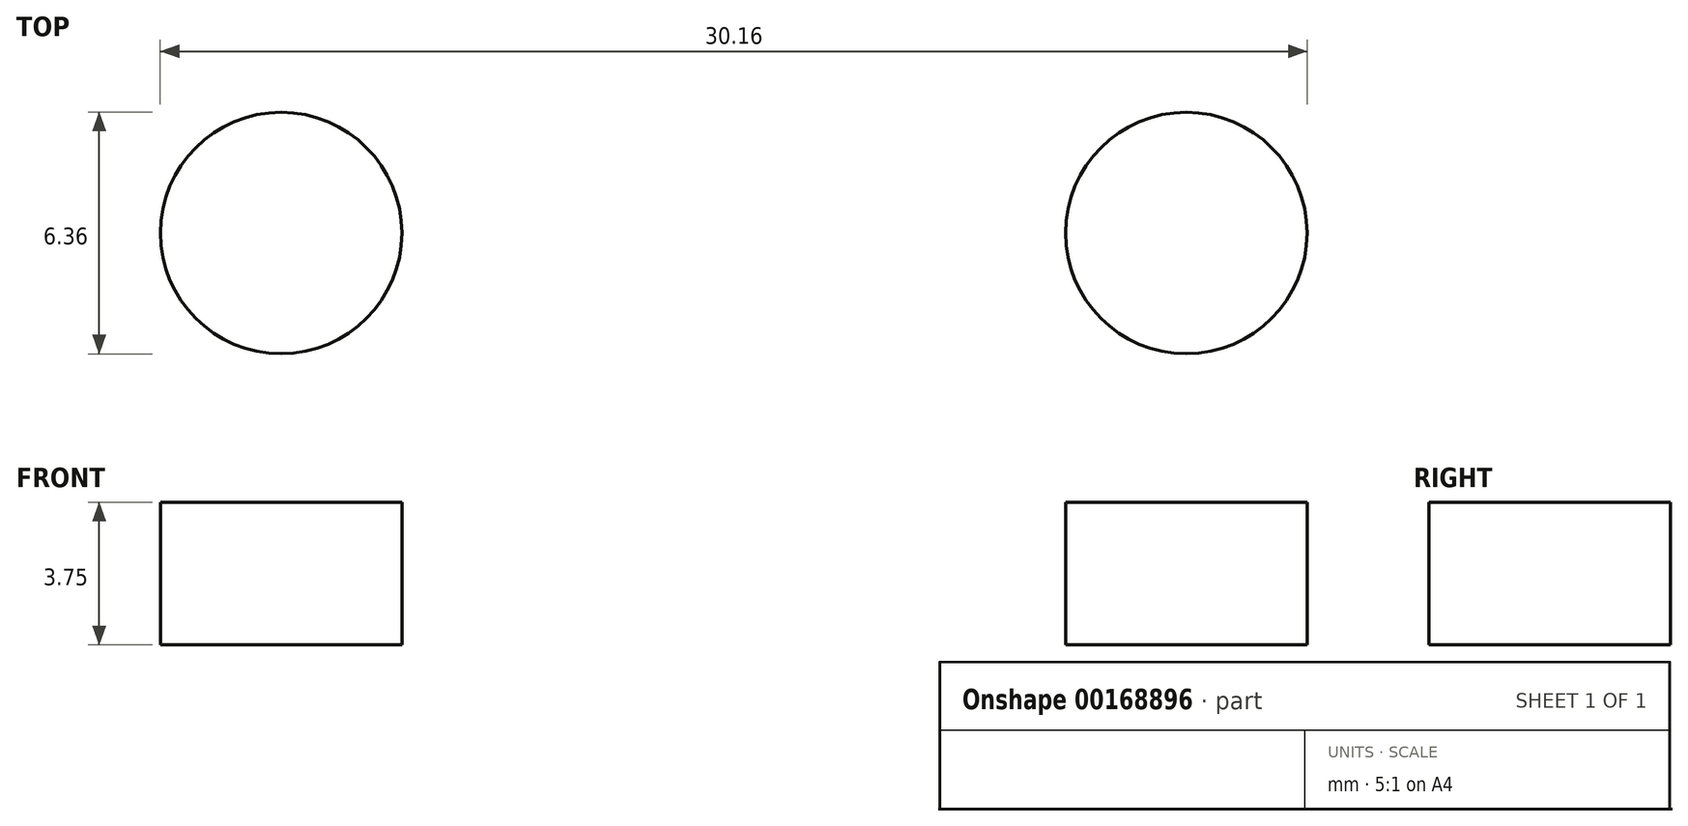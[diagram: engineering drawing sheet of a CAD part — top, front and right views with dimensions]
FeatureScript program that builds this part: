
annotation { "Feature Type Name" : "Feature", "Feature Type Description" : "" }
export const myFeature = defineFeature(function(context is Context, id is Id, definition is map)
    precondition{}
    {
        {
            var Q0;
            Q0=qCreatedBy(makeId("Top.planeOp"),FACE);
            var sketch = newSketch(context, id + "F0", { "sketchPlane" : qUnion([Q0])});
            skCircle(sketch, "E0", {"center": v(0, 0) * mm, "radius": 3.18 * mm});
            skSolve(sketch);
        }
        {
            var Q0;
            Q0=makeQuery(id+"F0.imprint","IMPRINT",FACE,{"disambiguationData":[TD([[makeQuery(id+"F0.imprint","IMPRINT",EDGE,{"derivedFrom":sQuery(id+"F0.wireOp",EDGE,"E0")}),1.0]])]});
            extrude(context, id + "F1", {"entities" : qUnion([Q0]), "depth" : 3.75 * mm});
        }
        {
            var Q0;
            Q0=makeQuery(id+"F1.opExtrude","SWEPT_BODY",BODY,{"disambiguationData":[OSD([sQuery(id+"F0.wireOp",EDGE,"E0")])]});
            transform(context, id + "F2", {"entities" : qUnion([Q0]), "transformType" : TransformType.TRANSLATION_3D, "dx" : -23.8 * mm, "dy" : 0 * mm, "dz" : 0 * mm, "makeCopy" : true});
        }
    });
